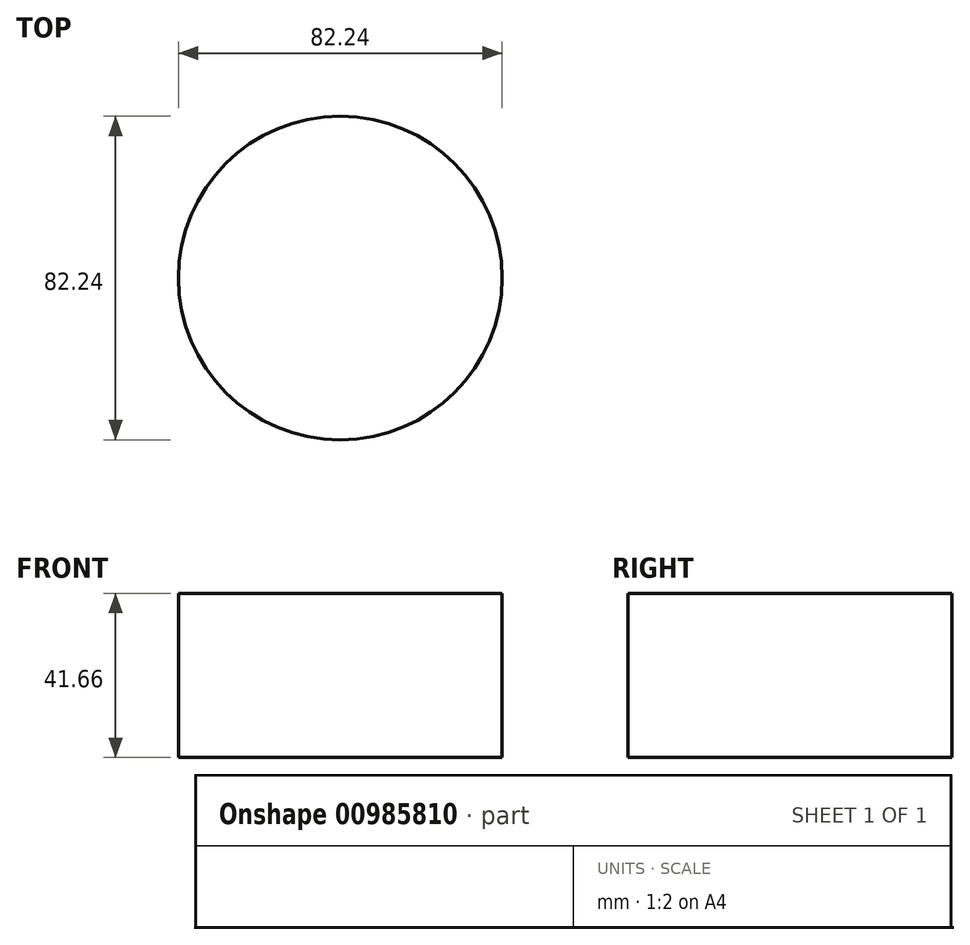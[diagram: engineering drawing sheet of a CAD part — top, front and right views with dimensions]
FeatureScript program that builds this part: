
annotation { "Feature Type Name" : "Feature", "Feature Type Description" : "" }
export const myFeature = defineFeature(function(context is Context, id is Id, definition is map)
    precondition{}
    {
        {
            var Q0;
            Q0=qCreatedBy(makeId("Top.planeOp"),FACE);
            var sketch = newSketch(context, id + "F0", { "sketchPlane" : qUnion([Q0])});
            skCircle(sketch, "E0", {"center": v(0, 0) * mm, "radius": 41.12 * mm});
            skSolve(sketch);
        }
        {
            var Q0;
            Q0=makeQuery(id+"F0.imprint","IMPRINT",FACE,{"disambiguationData":[TD([[makeQuery(id+"F0.imprint","IMPRINT",EDGE,{"derivedFrom":sQuery(id+"F0.wireOp",EDGE,"E0")}),1.0]])]});
            extrude(context, id + "F1", {"entities" : qUnion([Q0]), "depth" : 41.66 * mm, "offsetDistance" : 25.4 * mm});
        }
    });
